annotation { "Feature Type Name" : "Feature", "Feature Type Description" : "" }
export const myFeature = defineFeature(function(context is Context, id is Id, definition is map)
    precondition{}
    {
        {
            var Q0;
            Q0=qCreatedBy(makeId("Front.planeOp"),FACE);
            var sketch = newSketch(context, id + "F0", { "sketchPlane" : qUnion([Q0])});
            skLineSegment(sketch, "E0.bottom", {"start": v(57.15, -12.7) * mm, "end": v(-57.15, -12.7) * mm});
            skLineSegment(sketch, "E0.top", {"start": v(57.15, 12.7) * mm, "end": v(-57.15, 12.7) * mm});
            skLineSegment(sketch, "E0.left", {"start": v(57.15, -12.7) * mm, "end": v(57.15, 12.7) * mm});
            skLineSegment(sketch, "E0.right", {"start": v(-57.15, -12.7) * mm, "end": v(-57.15, 12.7) * mm});
            skPoint(sketch, "E0.middle", {"position": v(0, 0) * mm});
            skCircle(sketch, "E1", {"center": v(47.74, 0) * mm, "radius": 2.75 * mm});
            skSolve(sketch);
        }
        {
            var Q0;
            Q0 = qSketchRegion(id + "F0", true);
            extrude(context, id + "F1", {"entities" : qUnion([Q0]), "depth" : 2.54 * mm, "offsetDistance" : 25.4 * mm});
        }
        {
            var Q0;
            Q0=makeQuery(id+"F1.opExtrude","CAP_FACE",FACE,{"disambiguationData":[OSD([sQuery(id+"F0.wireOp",EDGE,"E0.bottom"),sQuery(id+"F0.wireOp",EDGE,"E0.top"),sQuery(id+"F0.wireOp",EDGE,"E0.left"),sQuery(id+"F0.wireOp",EDGE,"E0.right")])],"isStart":false});
            var sketch = newSketch(context, id + "F2", { "sketchPlane" : qUnion([Q0])});
            skText(sketch, "E2", { "text": "Panther Proud", "fontName": "OpenSans-Bold.ttf"});
            const initialGuessF2  = {"E2": [-0.05206, -0.00455, 1, 0, 0.00953]};
            skSetInitialGuess(sketch, initialGuessF2);
            skSolve(sketch);
        }
        {
            var Q0;
            Q0 = qSketchRegion(id + "F2", true);
            extrude(context, id + "F3", {"entities" : qUnion([Q0]), "operationType" : NewBodyOperationType.ADD, "depth" : 0.76 * mm, "offsetDistance" : 25.4 * mm});
        }
        {
            var Q0;
            Q0=makeQuery(id+"F1.opExtrude","SWEPT_EDGE",EDGE,{"disambiguationData":[OSD([sQuery(id+"F0.wireOp",EDGE,"E0.bottom"),sQuery(id+"F0.wireOp",EDGE,"E0.right")])]});
            fillet(context, id + "F4", {"entities" : qUnion([Q0]), "radius" : 3.17 * mm, "tangentPropagation" : true, "allowEdgeOverflow" : false});
        }
        {
            var Q0;
            Q0=makeQuery(id+"F1.opExtrude","SWEPT_EDGE",EDGE,{"disambiguationData":[OSD([sQuery(id+"F0.wireOp",EDGE,"E0.top"),sQuery(id+"F0.wireOp",EDGE,"E0.right")])]});
            fillet(context, id + "F5", {"entities" : qUnion([Q0]), "radius" : 3.17 * mm, "tangentPropagation" : true, "allowEdgeOverflow" : false});
        }
        {
            var Q0;
            Q0=makeQuery(id+"F1.opExtrude","SWEPT_EDGE",EDGE,{"disambiguationData":[OSD([sQuery(id+"F0.wireOp",EDGE,"E0.top"),sQuery(id+"F0.wireOp",EDGE,"E0.left")])]});
            fillet(context, id + "F6", {"entities" : qUnion([Q0]), "radius" : 3.17 * mm, "tangentPropagation" : true, "allowEdgeOverflow" : false});
        }
        {
            var Q0;
            Q0=makeQuery(id+"F1.opExtrude","SWEPT_EDGE",EDGE,{"disambiguationData":[OSD([sQuery(id+"F0.wireOp",EDGE,"E0.bottom"),sQuery(id+"F0.wireOp",EDGE,"E0.left")])]});
            fillet(context, id + "F7", {"entities" : qUnion([Q0]), "radius" : 3.17 * mm, "tangentPropagation" : true, "allowEdgeOverflow" : false});
        }
        {
            var Q0;
            Q0=makeQuery(id+"F3.opExtrude","CAP_FACE",FACE,{"disambiguationData":[OSD([sQuery(id+"F2.wireOp",EDGE,"E2.sketch_text.stroke-113"),sQuery(id+"F2.wireOp",EDGE,"E2.sketch_text.stroke-114"),sQuery(id+"F2.wireOp",EDGE,"E2.sketch_text.stroke-115"),sQuery(id+"F2.wireOp",EDGE,"E2.sketch_text.stroke-116"),sQuery(id+"F2.wireOp",EDGE,"E2.sketch_text.stroke-117"),sQuery(id+"F2.wireOp",EDGE,"E2.sketch_text.stroke-118"),sQuery(id+"F2.wireOp",EDGE,"E2.sketch_text.stroke-119"),sQuery(id+"F2.wireOp",EDGE,"E2.sketch_text.stroke-120"),sQuery(id+"F2.wireOp",EDGE,"E2.sketch_text.stroke-121"),sQuery(id+"F2.wireOp",EDGE,"E2.sketch_text.stroke-122"),sQuery(id+"F2.wireOp",EDGE,"E2.sketch_text.stroke-123"),sQuery(id+"F2.wireOp",EDGE,"E2.sketch_text.stroke-124"),sQuery(id+"F2.wireOp",EDGE,"E2.sketch_text.stroke-125")])],"isStart":false});
            var sketch = newSketch(context, id + "F8", { "sketchPlane" : qUnion([Q0])});
            skLineSegment(sketch, "E3.bottom", {"start": v(47.9, -8.83) * mm, "end": v(-47.9, -8.83) * mm});
            skLineSegment(sketch, "E3.top", {"start": v(47.9, 8.83) * mm, "end": v(-47.9, 8.83) * mm});
            skLineSegment(sketch, "E3.left", {"start": v(54.25, -2.48) * mm, "end": v(54.25, 2.48) * mm});
            skLineSegment(sketch, "E3.right", {"start": v(-54.25, -2.48) * mm, "end": v(-54.25, 2.48) * mm});
            skPoint(sketch, "E3.middle", {"position": v(0, 0) * mm});
            skLineSegment(sketch, "E4.0", {"start": v(53.98, 12.7) * mm, "end": v(-53.98, 12.7) * mm});
            skArc(sketch, "E5.0", {"start": v(-53.98, 12.7) * mm, "mid": v(-56.22, 11.77) * mm, "end": v(-57.15, 9.52) * mm});
            skLineSegment(sketch, "E6.0", {"start": v(-57.15, -9.52) * mm, "end": v(-57.15, 9.52) * mm});
            skPoint(sketch, "E7.0", {"position": v(-56.22, -11.77) * mm});
            skArc(sketch, "E8.0", {"start": v(-57.15, -9.52) * mm, "mid": v(-56.22, -11.77) * mm, "end": v(-53.98, -12.7) * mm});
            skLineSegment(sketch, "E9.0", {"start": v(53.98, -12.7) * mm, "end": v(-53.98, -12.7) * mm});
            skArc(sketch, "E10.0", {"start": v(53.98, -12.7) * mm, "mid": v(56.22, -11.77) * mm, "end": v(57.15, -9.52) * mm});
            skLineSegment(sketch, "E11.0.0", {"start": v(-53.98, -12.7) * mm, "end": v(53.98, -12.7) * mm});
            skLineSegment(sketch, "E11.0.2", {"start": v(57.15, -9.52) * mm, "end": v(57.15, 9.53) * mm});
            skArc(sketch, "E11.0.3", {"start": v(57.15, 9.53) * mm, "mid": v(56.22, 11.77) * mm, "end": v(53.98, 12.7) * mm});
            skLineSegment(sketch, "E11.0.6", {"start": v(-57.15, 9.52) * mm, "end": v(-57.15, -9.52) * mm});
            skPoint(sketch, "E12.visualSharp", {"position": v(-54.25, 8.83) * mm});
            skArc(sketch, "E12.filletArc", {"start": v(-47.9, 8.83) * mm, "mid": v(-52.4, 6.97) * mm, "end": v(-54.25, 2.48) * mm});
            skPoint(sketch, "E13.visualSharp", {"position": v(-54.25, -8.83) * mm});
            skArc(sketch, "E13.filletArc", {"start": v(-54.25, -2.48) * mm, "mid": v(-52.4, -6.97) * mm, "end": v(-47.9, -8.83) * mm});
            skPoint(sketch, "E14.visualSharp", {"position": v(54.25, 8.83) * mm});
            skArc(sketch, "E14.filletArc", {"start": v(54.25, 2.48) * mm, "mid": v(52.4, 6.97) * mm, "end": v(47.9, 8.83) * mm});
            skPoint(sketch, "E15.visualSharp", {"position": v(54.25, -8.83) * mm});
            skArc(sketch, "E15.filletArc", {"start": v(47.9, -8.83) * mm, "mid": v(52.4, -6.97) * mm, "end": v(54.25, -2.48) * mm});
            skSolve(sketch);
        }
        {
            var Q0;
            Q0=makeQuery(id+"F8.imprint","IMPRINT",FACE,{"disambiguationData":[TD([[makeQuery(id+"F8.imprint","IMPRINT",EDGE,{"derivedFrom":sQuery(id+"F8.wireOp",EDGE,"E3.bottom")}),1.0]])]});
            extrude(context, id + "F9", {"entities" : qUnion([Q0]), "depth" : 0.76 * mm, "offsetDistance" : 25.4 * mm});
        }
    });